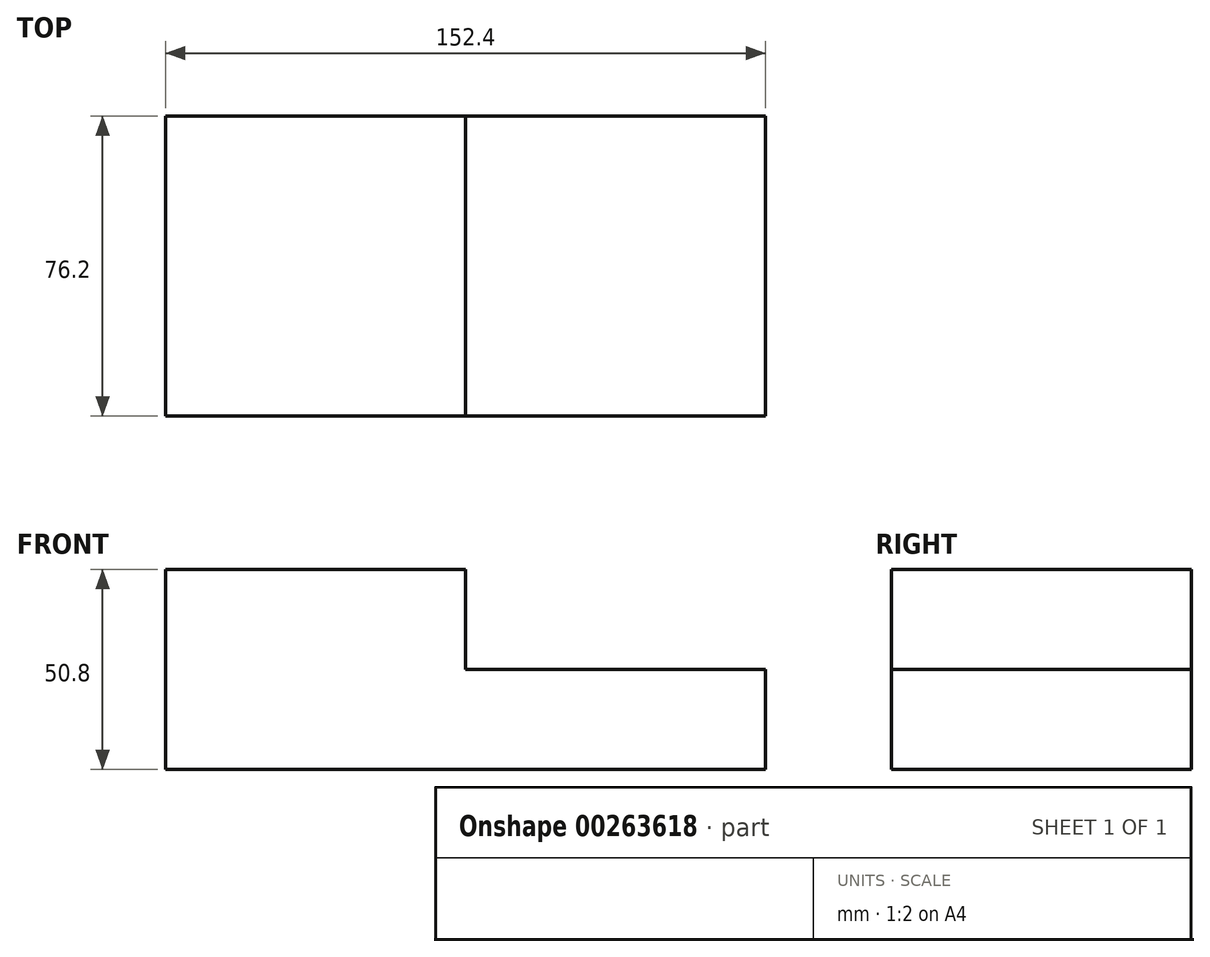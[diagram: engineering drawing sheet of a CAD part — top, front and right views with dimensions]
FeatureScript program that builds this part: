
annotation { "Feature Type Name" : "Feature", "Feature Type Description" : "" }
export const myFeature = defineFeature(function(context is Context, id is Id, definition is map)
    precondition{}
    {
        {
            var Q0;
            Q0=qCreatedBy(makeId("Front.planeOp"),FACE);
            var sketch = newSketch(context, id + "F0", { "sketchPlane" : qUnion([Q0])});
            skLineSegment(sketch, "E0", {"start": v(-75.45, 0) * mm, "end": v(-75.45, 50.8) * mm});
            skLineSegment(sketch, "E1", {"start": v(-75.45, 0) * mm, "end": v(76.95, 0) * mm});
            skLineSegment(sketch, "E2", {"start": v(-75.45, 50.8) * mm, "end": v(0.75, 50.8) * mm});
            skLineSegment(sketch, "E3", {"start": v(0.75, 50.8) * mm, "end": v(0.75, 25.4) * mm});
            skLineSegment(sketch, "E4", {"start": v(0.75, 25.4) * mm, "end": v(76.95, 25.4) * mm});
            skLineSegment(sketch, "E5", {"start": v(76.95, 25.4) * mm, "end": v(76.95, 0) * mm});
            skSolve(sketch);
        }
        {
            var Q0;
            Q0=makeQuery(id+"F0.imprint","IMPRINT",FACE,{"disambiguationData":[TD([[makeQuery(id+"F0.imprint","IMPRINT",EDGE,{"derivedFrom":sQuery(id+"F0.wireOp",EDGE,"E0")}),-1.0]])]});
            extrude(context, id + "F1", {"entities" : qUnion([Q0]), "depth" : 76.2 * mm});
        }
    });
